# Revit family: Geberit Selnova klozet kapağı, üstten sabitlemeli_PRO_335824
name_source: partatom
category: Furniture
units: mm (PartAtom-declared; Revit-internal decimal feet)

## family parameters
Always vertical = Yes
Cut with Voids When Loaded = No
OmniClass Number = 23.40.20.21
OmniClass Title = Toilet and Bath Specialties
Room Calculation Point = Yes
Shared = No
Work Plane-Based = No

## types (1)
- 500.335.01.1 Geberit Selnova klozet kapağı, üstten sabitlemeli
    500330_0_view = Yes
    Application range = Furniture
    Article number key = 500.335.01.1
    BIM Content Version = GEB MG 1.2
    BIM Content revision date = 2020.05.18
    Brand = Geberit
    CW Connection = Yes
    Characteristics = Tam kapanan klozet kapağı
Metal menteşeler
    Default Elevation = 0 mm  [stored 0 ft]
    Description = Geberit Selnova klozet kapağı, üstten sabitlemeli
    EAN code basic data = 4025416531838
    GEB_culture = tr-TR
    GEB_generic_description = GBC
    GEB_generic_manufacturer = generic
    GEB_pimversion = 23.02.17
    GEB_processing_type = T
    GEB_reference = PRO_335824
    GEB_translations = {"ATT_10673":"EAN code basic data","ATT_459792":"Renk / Yüzey","applicationPurposes":"Application purposes","application_range":"Application range","brandName":"Brand","characteristics":"Characteristics","content_creator":"BIM Content creator","content_date_changed":"BIM Content revision date","content_version":"BIM Content Version","key 1000":"Article number key","name":"Name","productBrand":"Product brand","scopeOfDelivery":"Scope of delivery","type":"Type","fixed_material":"Main material"}
    HW Connection = No
    IfcDescription = Geberit Selnova klozet kapağı, üstten sabitlemeli
    IfcExportAs = IfcSanitaryTerminal
    IfcExportType = WCSEAT
    LOD300 = No
    LOD400 = Yes
    Main material = Geberit, Plastic, Opaque white
    Manufacturer = Geberit
    Name = Geberit Selnova klozet kapağı, üstten sabitlemeli
    Renk / Yüzey = Beyaz / Parlak
    Scope of delivery = Klozet kapağı
    Vent Connection = No
    Waste Connection = Yes

note: [stored X ft] marks values corroborated as IEEE doubles in the binary element streams (Revit-internal decimal feet)

## geometry (parser evidence)
native form markers: Blend x8, Sweep x11
no freeform markers — native parametric forms only
